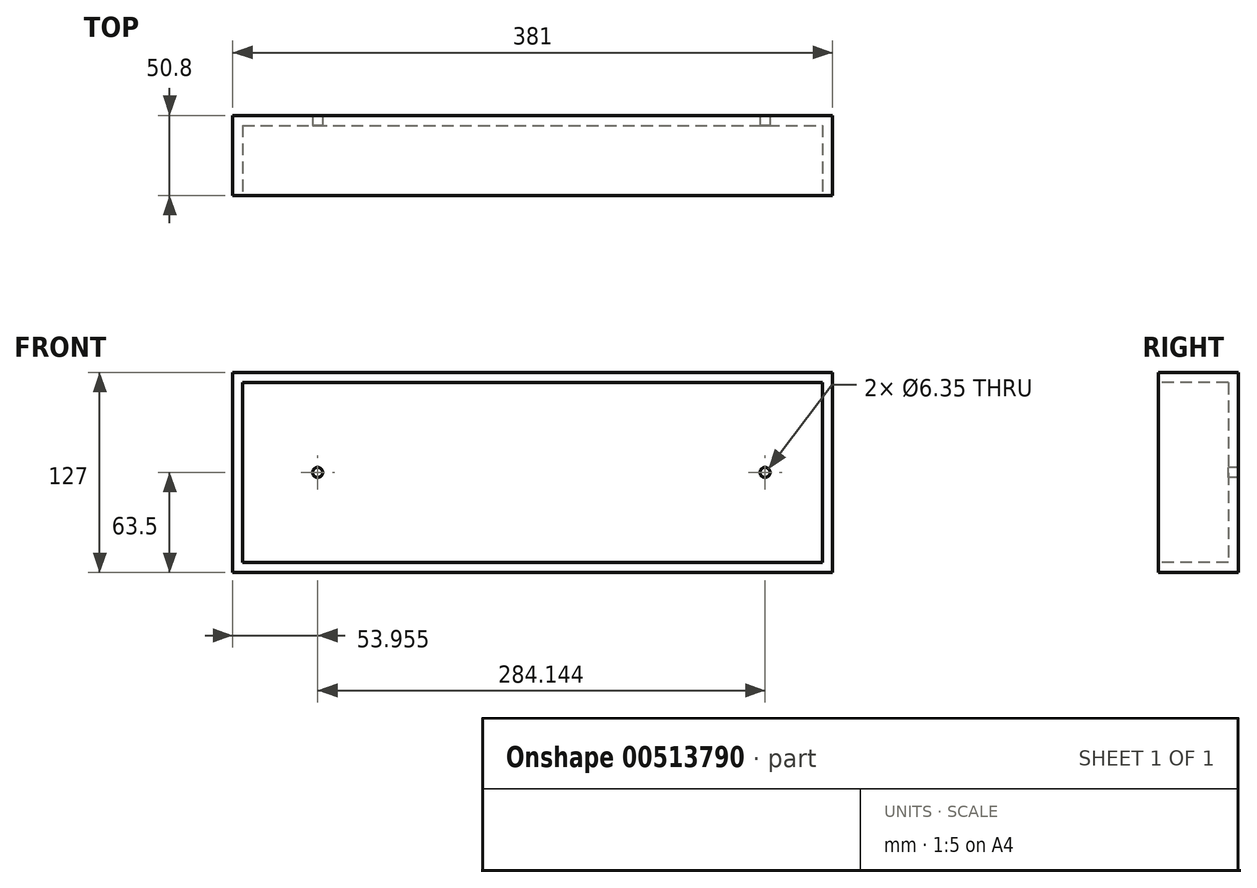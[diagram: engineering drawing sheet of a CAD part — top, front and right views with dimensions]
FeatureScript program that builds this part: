
annotation { "Feature Type Name" : "Feature", "Feature Type Description" : "" }
export const myFeature = defineFeature(function(context is Context, id is Id, definition is map)
    precondition{}
    {
        {
            var Q0;
            Q0=qCreatedBy(makeId("Front.planeOp"),FACE);
            var sketch = newSketch(context, id + "F0", { "sketchPlane" : qUnion([Q0])});
            skLineSegment(sketch, "E0.bottom", {"start": v(0, 0) * mm, "end": v(381, 0) * mm});
            skLineSegment(sketch, "E0.top", {"start": v(0, 127) * mm, "end": v(381, 127) * mm});
            skLineSegment(sketch, "E0.left", {"start": v(0, 0) * mm, "end": v(0, 127) * mm});
            skLineSegment(sketch, "E0.right", {"start": v(381, 0) * mm, "end": v(381, 127) * mm});
            skSolve(sketch);
        }
        {
            var Q0;
            Q0 = qSketchRegion(id + "F0", true);
            extrude(context, id + "F1", {"entities" : qUnion([Q0]), "oppositeDirection" : true, "depth" : 50.8 * mm, "offsetDistance" : 25.4 * mm});
        }
        {
            var Q0;
            Q0=makeQuery(id+"F1.opExtrude","CAP_FACE",FACE,{"disambiguationData":[OSD([sQuery(id+"F0.wireOp",EDGE,"E0.bottom"),sQuery(id+"F0.wireOp",EDGE,"E0.top"),sQuery(id+"F0.wireOp",EDGE,"E0.left"),sQuery(id+"F0.wireOp",EDGE,"E0.right")])],"isStart":true});
            var sketch = newSketch(context, id + "F2", { "sketchPlane" : qUnion([Q0])});
            skLineSegment(sketch, "E1.bottom", {"start": v(6.35, 120.65) * mm, "end": v(374.65, 120.65) * mm});
            skLineSegment(sketch, "E1.top", {"start": v(6.35, 6.35) * mm, "end": v(374.65, 6.35) * mm});
            skLineSegment(sketch, "E1.left", {"start": v(6.35, 120.65) * mm, "end": v(6.35, 6.35) * mm});
            skLineSegment(sketch, "E1.right", {"start": v(374.65, 120.65) * mm, "end": v(374.65, 6.35) * mm});
            skSolve(sketch);
        }
        {
            var Q0;
            Q0=makeQuery(id+"F2.imprint","IMPRINT",FACE,{"disambiguationData":[TD([[makeQuery(id+"F2.imprint","IMPRINT",EDGE,{"derivedFrom":sQuery(id+"F2.wireOp",EDGE,"E1.bottom")}),-1.0]])]});
            extrude(context, id + "F3", {"entities" : qUnion([Q0]), "operationType" : NewBodyOperationType.REMOVE, "oppositeDirection" : true, "depth" : 44.45 * mm, "offsetDistance" : 25.4 * mm});
        }
        {
            var Q0;
            Q0=makeQuery(id+"F3.boolean.opBoolean","COPY",FACE,{"derivedFrom":makeQuery(id+"F3.opExtrude","CAP_FACE",FACE,{"disambiguationData":[OSD([sQuery(id+"F2.wireOp",EDGE,"E1.bottom"),sQuery(id+"F2.wireOp",EDGE,"E1.top"),sQuery(id+"F2.wireOp",EDGE,"E1.left"),sQuery(id+"F2.wireOp",EDGE,"E1.right")])],"isStart":false})});
            var sketch = newSketch(context, id + "F4", { "sketchPlane" : qUnion([Q0])});
            skCircle(sketch, "E2", {"center": v(53.96, 63.5) * mm, "radius": 3.18 * mm});
            skCircle(sketch, "E3", {"center": v(338.1, 63.5) * mm, "radius": 3.18 * mm});
            skSolve(sketch);
        }
        {
            var Q0;
            Q0=makeQuery(id+"F4.imprint","IMPRINT",FACE,{"disambiguationData":[TD([[makeQuery(id+"F4.imprint","IMPRINT",EDGE,{"derivedFrom":sQuery(id+"F4.wireOp",EDGE,"E2")}),1.0]])]});
            var Q1;
            Q1=makeQuery(id+"F4.imprint","IMPRINT",FACE,{"disambiguationData":[TD([[makeQuery(id+"F4.imprint","IMPRINT",EDGE,{"derivedFrom":sQuery(id+"F4.wireOp",EDGE,"E3")}),1.0]])]});
            extrude(context, id + "F5", {"entities" : qUnion([Q0, Q1]), "operationType" : NewBodyOperationType.REMOVE, "endBound" : BoundingType.THROUGH_ALL, "oppositeDirection" : true, "depth" : 25.4 * mm, "offsetDistance" : 25.4 * mm});
        }
    });
